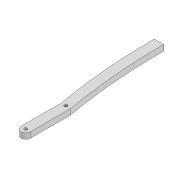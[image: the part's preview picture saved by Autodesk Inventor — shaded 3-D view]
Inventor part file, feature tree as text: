
AUTODESK INVENTOR PART (.ipt)
format: ipt  version: 2022 (Build 260153000, 153)  size: 112,128 bytes
history: native  units: mm
features: extrude x2, sketch x2
ambient origin geometry x8: Origin, YZ Plane, XZ Plane, XY Plane, X Axis, Y Axis, Z Axis, Center Point
bodies: Solid1 (feature_tree)
feature tree (4):
  extrude  "Extrusion1"  Depth=3.3mm
  extrude  "Extrusion2"  Depth=10.0mm
  sketch  "Sketch1"  dims[d0=3.3mm d1=3.3mm]
  sketch  "Sketch2"  dims[d2=10.0mm d3=312.648mm d6=6.0mm d7=0.0mm d10=3.3mm d11=42.6mm d12=3.3mm d13=254.274mm d16=600.0mm d17=600.0mm d18=10.0mm d19=0.0mm]
